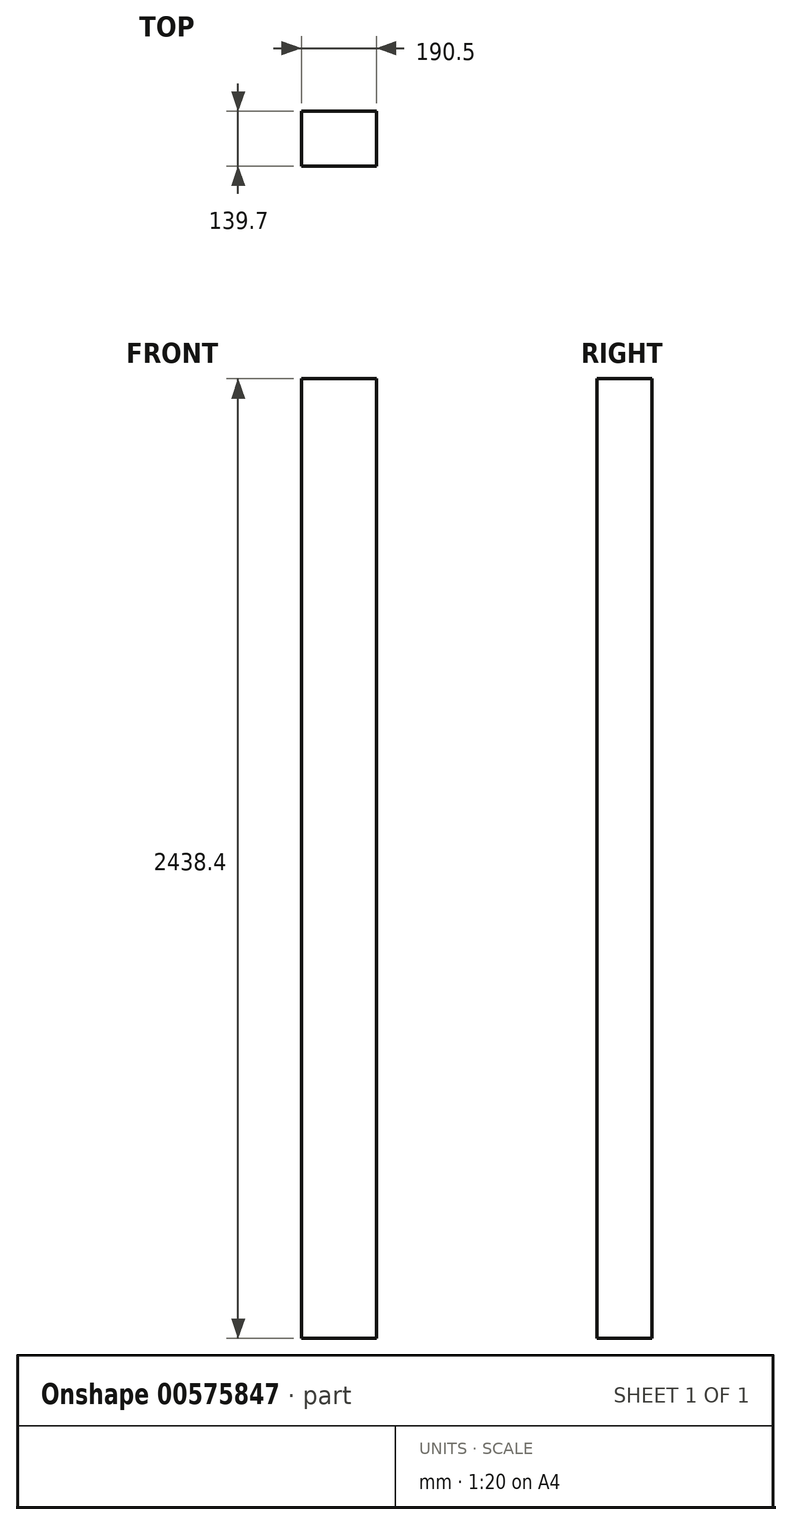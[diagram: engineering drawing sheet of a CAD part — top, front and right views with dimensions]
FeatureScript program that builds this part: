
annotation { "Feature Type Name" : "Feature", "Feature Type Description" : "" }
export const myFeature = defineFeature(function(context is Context, id is Id, definition is map)
    precondition{}
    {
        {
            var Q0;
            Q0=qCreatedBy(makeId("Top.planeOp"),FACE);
            var sketch = newSketch(context, id + "F0", { "sketchPlane" : qUnion([Q0])});
            skLineSegment(sketch, "E0.bottom", {"start": v(0, 0) * mm, "end": v(190.5, 0) * mm});
            skLineSegment(sketch, "E0.top", {"start": v(0, 139.7) * mm, "end": v(190.5, 139.7) * mm});
            skLineSegment(sketch, "E0.left", {"start": v(0, 0) * mm, "end": v(0, 139.7) * mm});
            skLineSegment(sketch, "E0.right", {"start": v(190.5, 0) * mm, "end": v(190.5, 139.7) * mm});
            skSolve(sketch);
        }
        {
            var Q0;
            Q0=qSketchRegion(id+"F0",true);
            extrude(context, id + "F1", {"entities" : qUnion([Q0]), "depth" : 2438.4 * mm, "offsetDistance" : 25.4 * mm});
        }
    });
